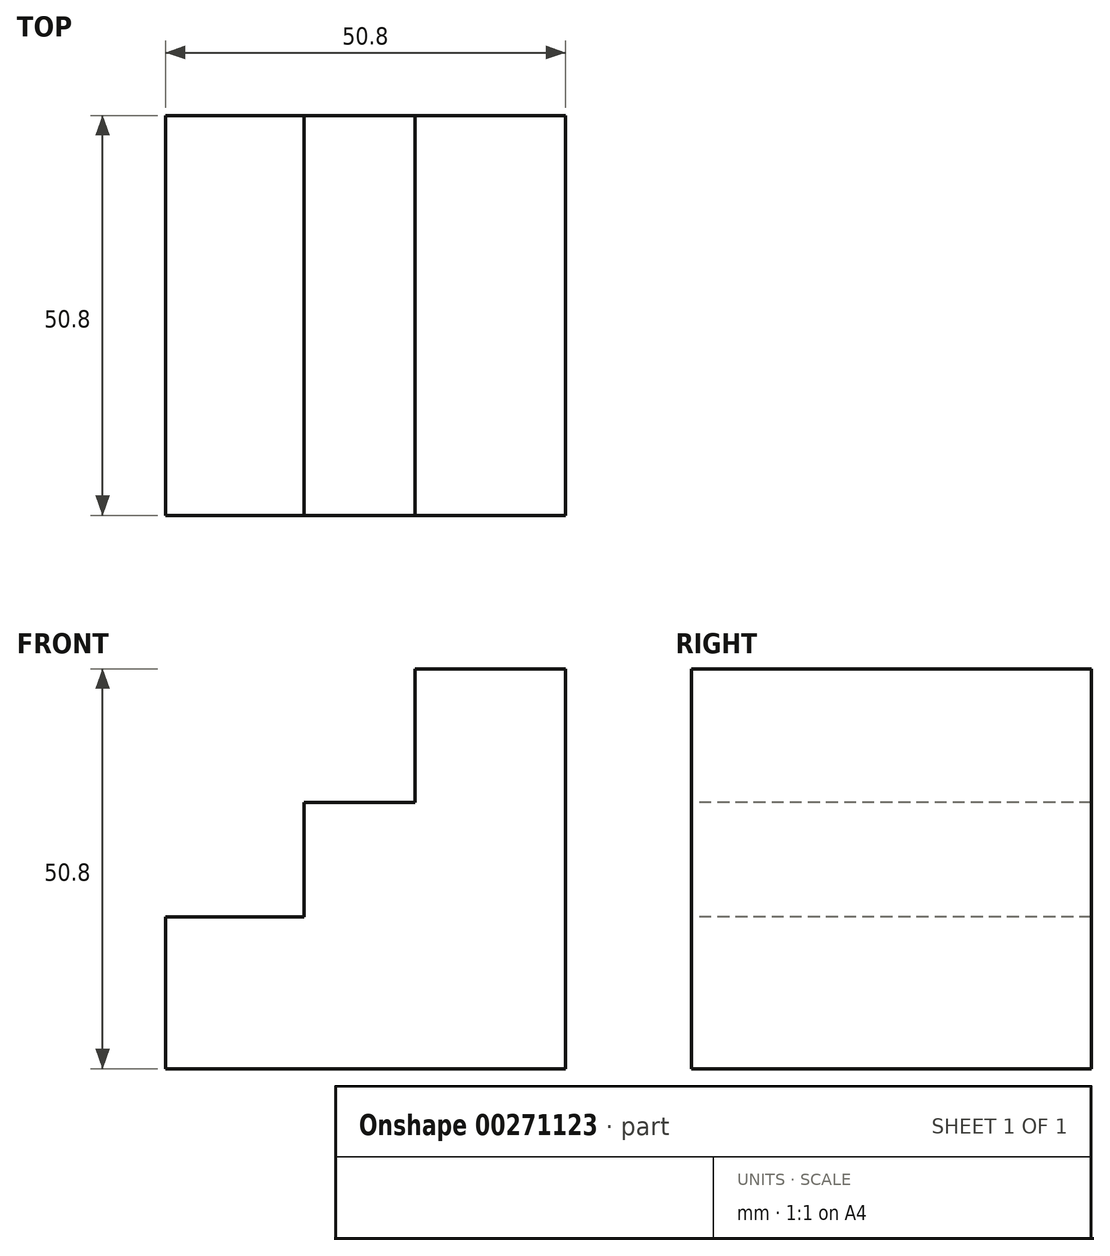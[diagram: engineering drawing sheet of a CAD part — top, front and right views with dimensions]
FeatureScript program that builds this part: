
annotation { "Feature Type Name" : "Feature", "Feature Type Description" : "" }
export const myFeature = defineFeature(function(context is Context, id is Id, definition is map)
    precondition{}
    {
        {
            var Q0;
            Q0=qCreatedBy(makeId("Front.planeOp"),FACE);
            var sketch = newSketch(context, id + "F0", { "sketchPlane" : qUnion([Q0])});
            skLineSegment(sketch, "E0.bottom", {"start": v(0, 0) * mm, "end": v(-50.8, 0) * mm});
            skLineSegment(sketch, "E0.top", {"start": v(0, 50.8) * mm, "end": v(-50.8, 50.8) * mm});
            skLineSegment(sketch, "E0.left", {"start": v(0, 0) * mm, "end": v(0, 50.8) * mm});
            skLineSegment(sketch, "E0.right", {"start": v(-50.8, 0) * mm, "end": v(-50.8, 50.8) * mm});
            skSolve(sketch);
        }
        {
            var Q0;
            Q0=makeQuery(id+"F0.imprint","IMPRINT",FACE,{"disambiguationData":[TD([[makeQuery(id+"F0.imprint","IMPRINT",EDGE,{"derivedFrom":sQuery(id+"F0.wireOp",EDGE,"E0.bottom")}),-1.0]])]});
            extrude(context, id + "F1", {"entities" : qUnion([Q0]), "depth" : 50.8 * mm});
        }
        {
            var Q0;
            Q0=makeQuery(id+"F1.opExtrude","CAP_FACE",FACE,{"disambiguationData":[OSD([sQuery(id+"F0.wireOp",EDGE,"E0.bottom"),sQuery(id+"F0.wireOp",EDGE,"E0.top"),sQuery(id+"F0.wireOp",EDGE,"E0.left"),sQuery(id+"F0.wireOp",EDGE,"E0.right")])],"isStart":false});
            var sketch = newSketch(context, id + "F2", { "sketchPlane" : qUnion([Q0])});
            skLineSegment(sketch, "E1", {"start": v(-50.8, 0) * mm, "end": v(-50.8, 50.8) * mm});
            skLineSegment(sketch, "E2", {"start": v(-50.8, 50.8) * mm, "end": v(-19.1, 50.8) * mm});
            skLineSegment(sketch, "E3", {"start": v(-19.1, 50.8) * mm, "end": v(-19.1, 33.8) * mm});
            skLineSegment(sketch, "E4", {"start": v(-19.1, 33.8) * mm, "end": v(-33.23, 33.8) * mm});
            skLineSegment(sketch, "E5", {"start": v(-33.23, 33.8) * mm, "end": v(-33.23, 19.29) * mm});
            skLineSegment(sketch, "E6", {"start": v(-33.23, 19.29) * mm, "end": v(-50.8, 19.29) * mm});
            skLineSegment(sketch, "E7", {"start": v(-50.8, 19.29) * mm, "end": v(-50.8, 50.8) * mm});
            skSolve(sketch);
        }
        {
            var Q0;
            Q0=makeQuery(id+"F2.imprint","IMPRINT",FACE,{"disambiguationData":[TD([[makeQuery(id+"F2.imprint","IMPRINT",EDGE,{"derivedFrom":sQuery(id+"F2.wireOp",EDGE,"E2")}),1.0]])]});
            extrude(context, id + "F3", {"entities" : qUnion([Q0]), "operationType" : NewBodyOperationType.REMOVE, "oppositeDirection" : true, "depth" : 50.8 * mm});
        }
    });
